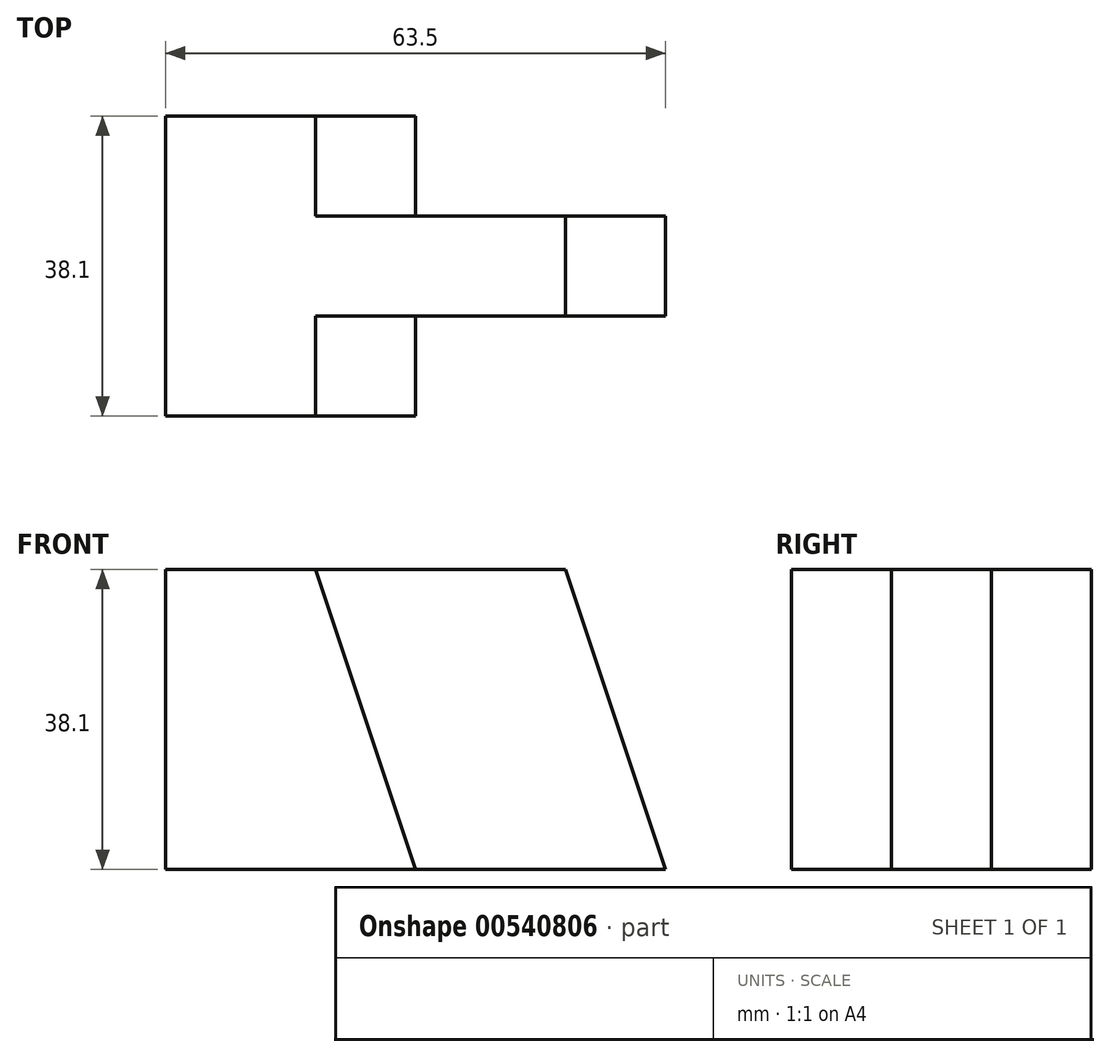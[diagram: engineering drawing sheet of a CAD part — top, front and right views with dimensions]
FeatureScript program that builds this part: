
annotation { "Feature Type Name" : "Feature", "Feature Type Description" : "" }
export const myFeature = defineFeature(function(context is Context, id is Id, definition is map)
    precondition{}
    {
        {
            var Q0;
            Q0=qCreatedBy(makeId("Front.planeOp"),FACE);
            var sketch = newSketch(context, id + "F0", { "sketchPlane" : qUnion([Q0])});
            skLineSegment(sketch, "E0", {"start": v(0, 0) * mm, "end": v(57.15, 0) * mm});
            skLineSegment(sketch, "E1", {"start": v(57.15, 0) * mm, "end": v(57.15, 38.1) * mm});
            skLineSegment(sketch, "E2", {"start": v(57.15, 38.1) * mm, "end": v(0, 38.1) * mm});
            skLineSegment(sketch, "E3", {"start": v(0, 38.1) * mm, "end": v(0, 0) * mm});
            skSolve(sketch);
        }
        {
            var Q0;
            Q0=makeQuery(id+"F0.imprint","IMPRINT",FACE,{"disambiguationData":[TD([[makeQuery(id+"F0.imprint","IMPRINT",EDGE,{"derivedFrom":sQuery(id+"F0.wireOp",EDGE,"E0")}),1.0]])]});
            extrude(context, id + "F1", {"entities" : qUnion([Q0]), "depth" : 38.1 * mm, "offsetDistance" : 25.4 * mm});
        }
        {
            var Q0;
            Q0=makeQuery(id+"F1.opExtrude","CAP_FACE",FACE,{"disambiguationData":[OSD([sQuery(id+"F0.wireOp",EDGE,"E0"),sQuery(id+"F0.wireOp",EDGE,"E1"),sQuery(id+"F0.wireOp",EDGE,"E2"),sQuery(id+"F0.wireOp",EDGE,"E3")])],"isStart":false});
            var sketch = newSketch(context, id + "F2", { "sketchPlane" : qUnion([Q0])});
            skLineSegment(sketch, "E4", {"start": v(25.4, 0) * mm, "end": v(12.7, 38.1) * mm});
            skLineSegment(sketch, "E5", {"start": v(12.7, 38.1) * mm, "end": v(25.4, 38.1) * mm});
            skLineSegment(sketch, "E6", {"start": v(25.4, 38.1) * mm, "end": v(25.4, 0) * mm});
            skSolve(sketch);
        }
        {
            var Q0;
            {var subQ0=sQuery(id+"F2.wireOp",EDGE,"E6");Q0=makeQuery(id+"F2.imprint","IMPRINT",FACE,{"disambiguationData":[TD([[makeQuery(id+"F2.imprint","IMPRINT",EDGE,{"derivedFrom":subQ0}),1.0]])]});}
            var Q1;
            Q1=makeQuery(id+"F2.imprint","IMPRINT",FACE,{"disambiguationData":[TD([[makeQuery(id+"F2.imprint","IMPRINT",EDGE,{"derivedFrom":sQuery(id+"F2.wireOp",EDGE,"E4")}),-1.0]])]});
            extrude(context, id + "F3", {"entities" : qUnion([Q0, Q1]), "operationType" : NewBodyOperationType.REMOVE, "oppositeDirection" : true, "depth" : 12.7 * mm, "offsetDistance" : 25.4 * mm});
        }
        {
            var Q0;
            Q0=makeQuery(id+"F3.boolean.opBoolean","COPY",FACE,{"derivedFrom":makeQuery(id+"F3.opExtrude","CAP_FACE",FACE,{"disambiguationData":[OSD([sQuery(id+"F0.wireOp",EDGE,"E0"),sQuery(id+"F0.wireOp",EDGE,"E1"),sQuery(id+"F0.wireOp",EDGE,"E2"),sQuery(id+"F2.wireOp",EDGE,"E4"),sQuery(id+"F2.wireOp",EDGE,"E5")])],"isStart":false})});
            var sketch = newSketch(context, id + "F4", { "sketchPlane" : qUnion([Q0])});
            skLineSegment(sketch, "E7", {"start": v(57.15, 0) * mm, "end": v(44.45, 38.1) * mm});
            skLineSegment(sketch, "E8", {"start": v(44.45, 38.1) * mm, "end": v(57.15, 38.1) * mm});
            skLineSegment(sketch, "E9", {"start": v(57.15, 38.1) * mm, "end": v(57.15, 0) * mm});
            skSolve(sketch);
        }
        {
            var Q0;
            Q0=makeQuery(id+"F4.imprint","IMPRINT",FACE,{"disambiguationData":[TD([[makeQuery(id+"F4.imprint","IMPRINT",EDGE,{"derivedFrom":sQuery(id+"F4.wireOp",EDGE,"E7")}),-1.0]])]});
            extrude(context, id + "F5", {"entities" : qUnion([Q0]), "operationType" : NewBodyOperationType.REMOVE, "oppositeDirection" : true, "depth" : 12.7 * mm, "offsetDistance" : 25.4 * mm});
        }
        {
            var Q0;
            Q0=makeQuery(id+"F1.opExtrude","CAP_FACE",FACE,{"disambiguationData":[OSD([sQuery(id+"F0.wireOp",EDGE,"E0"),sQuery(id+"F0.wireOp",EDGE,"E1"),sQuery(id+"F0.wireOp",EDGE,"E2"),sQuery(id+"F0.wireOp",EDGE,"E3")])],"isStart":true});
            var sketch = newSketch(context, id + "F6", { "sketchPlane" : qUnion([Q0])});
            skLineSegment(sketch, "E10", {"start": v(-25.4, 38.1) * mm, "end": v(-25.4, 0) * mm});
            skLineSegment(sketch, "E11", {"start": v(-25.4, 0) * mm, "end": v(-12.7, 38.1) * mm});
            skLineSegment(sketch, "E12", {"start": v(-12.7, 38.1) * mm, "end": v(-25.4, 38.1) * mm});
            skSolve(sketch);
        }
        {
            var Q0;
            {var subQ0=sQuery(id+"F6.wireOp",EDGE,"E10");Q0=makeQuery(id+"F6.imprint","IMPRINT",FACE,{"disambiguationData":[TD([[makeQuery(id+"F6.imprint","IMPRINT",EDGE,{"derivedFrom":subQ0}),-1.0]])]});}
            var Q1;
            Q1=makeQuery(id+"F6.imprint","IMPRINT",FACE,{"disambiguationData":[TD([[makeQuery(id+"F6.imprint","IMPRINT",EDGE,{"derivedFrom":sQuery(id+"F6.wireOp",EDGE,"E10")}),1.0]])]});
            extrude(context, id + "F7", {"entities" : qUnion([Q0, Q1]), "operationType" : NewBodyOperationType.REMOVE, "oppositeDirection" : true, "depth" : 12.7 * mm, "offsetDistance" : 25.4 * mm});
        }
        {
            var Q0;
            Q0=makeQuery(id+"F1.opExtrude","SWEPT_FACE",FACE,{"disambiguationData":[OSD([sQuery(id+"F0.wireOp",EDGE,"E3")])]});
            extrude(context, id + "F8", {"entities" : qUnion([Q0]), "operationType" : NewBodyOperationType.ADD, "depth" : 6.35 * mm, "offsetDistance" : 25.4 * mm});
        }
    });
